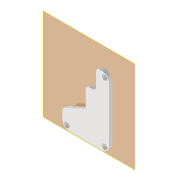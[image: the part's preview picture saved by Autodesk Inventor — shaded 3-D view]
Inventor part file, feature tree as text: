
AUTODESK INVENTOR PART (.ipt)
format: ipt  version: 2022 (Build 260153000, 153)  size: 212,992 bytes
history: native  units: mm
features: reference x5, extrude x4, other x4, sketch x3, plane x2, fillet x2, projected_geometry x2, hole x1
ambient origin geometry x8: Origin, YZ Plane, XZ Plane, XY Plane, X Axis, Y Axis, Z Axis, Center Point
bodies: Volumenkörper1 (feature_tree)
feature tree (23):
  plane  "Arbeitsebene1"
  extrude  "Extrusion1"  Depth=2.0mm
  plane  "Arbeitsebene2"
  hole  "Bohrung1"  [1 undecoded]
  extrude  "Extrusion2"  Depth=3.0mm TaperAngle=0.0deg
  fillet  "Rundung2"  Radius=4.0mm
  extrude  "Extrusion3"  Depth=10.0mm TaperAngle=0.0deg
  extrude  "Extrusion4"  Depth=10.0mm TaperAngle=0.0deg
  fillet  "Rundung3"  Radius=2.0mm
  reference  "Referenz9"
  reference  "Referenz10"
  projected_geometry  "Projizierte Kontur3"
  sketch  "Skizze4"  dims[d2=2.0mm d3=0.0mm]
  reference  "Referenz11"
  reference  "Referenz12"
  sketch  "Skizze5"  dims[d4=3.2mm d5=6.0mm d6=4.0mm d7=2.0mm d8=90.0deg d9=8.0mm d10=20.594885mm d21=2.5mm]
  reference  "Referenz13"
  sketch  "Skizze6"  dims[d22=0.5mm d23=0.5mm d24=3.0mm d25=0.0mm d26=4.0mm d27=10.0mm d28=0.0mm d29=10.0mm d30=0.0mm d31=2.0mm]
  projected_geometry  "Projizierte Kontur4"
  other  "Baugruppe5"
  other  "00_ESP32_XIAO_Adapter_base_a4988:1"
  other  "Assembly_Cube_SEEED_Xiao_Sense_Camera_v3.iam"
  other  "20_Cube_Insert_SEEED_Xiao_Sense_Camera:1"
note: 1 required parameter value undecoded (feature->parameter linkage not recoverable at this tier; creation-order binding heuristic only, values carry confidence <= 0.55)
